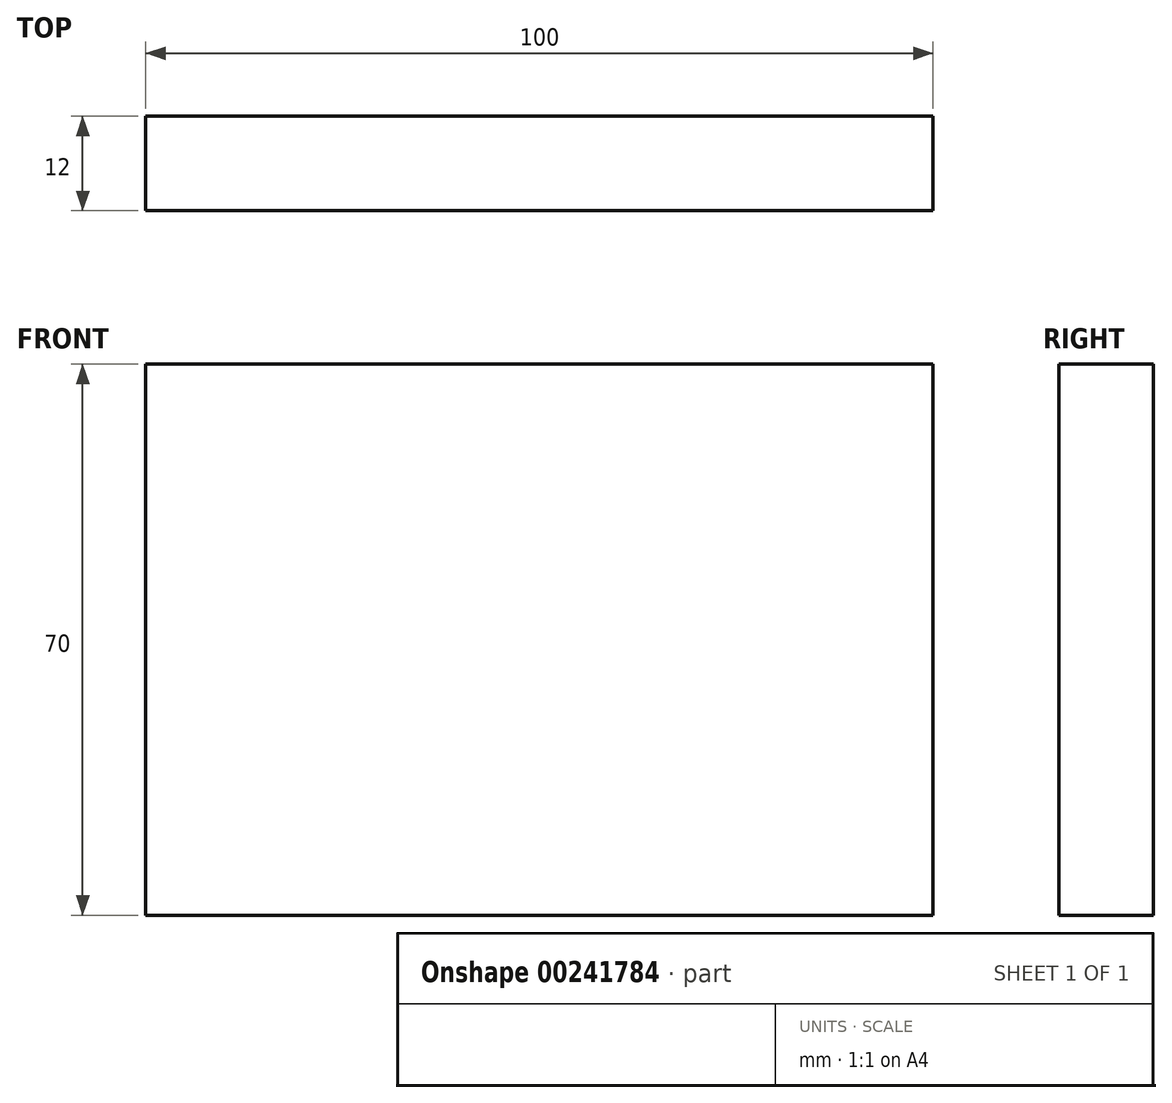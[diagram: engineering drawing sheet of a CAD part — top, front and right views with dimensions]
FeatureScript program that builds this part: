
annotation { "Feature Type Name" : "Feature", "Feature Type Description" : "" }
export const myFeature = defineFeature(function(context is Context, id is Id, definition is map)
    precondition{}
    {
        {
            var Q0;
            Q0=qCreatedBy(makeId("Front.planeOp"),FACE);
            var sketch = newSketch(context, id + "F0", { "sketchPlane" : qUnion([Q0])});
            skLineSegment(sketch, "E0.bottom", {"start": v(0, 0) * mm, "end": v(100, 0) * mm});
            skLineSegment(sketch, "E0.top", {"start": v(0, 70) * mm, "end": v(100, 70) * mm});
            skLineSegment(sketch, "E0.left", {"start": v(0, 0) * mm, "end": v(0, 70) * mm});
            skLineSegment(sketch, "E0.right", {"start": v(100, 0) * mm, "end": v(100, 70) * mm});
            skSolve(sketch);
        }
        {
            var Q0;
            Q0=qSketchRegion(id+"F0",true);
            extrude(context, id + "F1", {"entities" : qUnion([Q0]), "depth" : 12 * mm});
        }
    });
